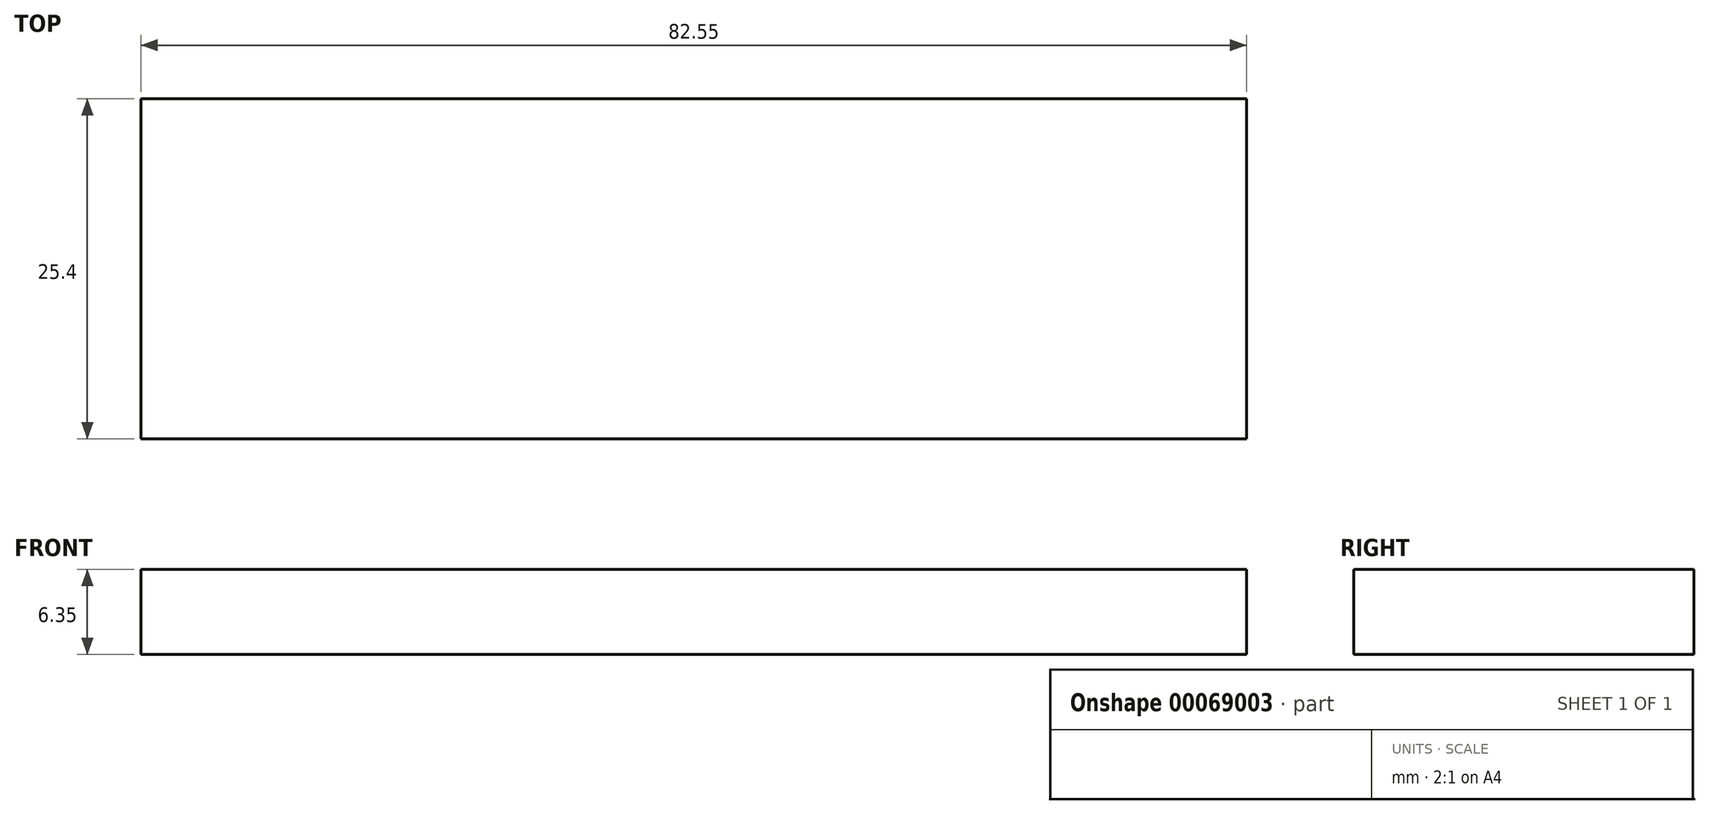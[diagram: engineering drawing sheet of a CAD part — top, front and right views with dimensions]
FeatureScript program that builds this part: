
annotation { "Feature Type Name" : "Feature", "Feature Type Description" : "" }
export const myFeature = defineFeature(function(context is Context, id is Id, definition is map)
    precondition{}
    {
        {
            var Q0;
            Q0=qCreatedBy(makeId("Top.planeOp"),FACE);
            var sketch = newSketch(context, id + "F0", { "sketchPlane" : qUnion([Q0])});
            skLineSegment(sketch, "E0.bottom", {"start": v(-45.02, 11.49) * mm, "end": v(37.53, 11.49) * mm});
            skLineSegment(sketch, "E0.top", {"start": v(-45.02, -13.91) * mm, "end": v(37.53, -13.91) * mm});
            skLineSegment(sketch, "E0.left", {"start": v(-45.02, 11.49) * mm, "end": v(-45.02, -13.91) * mm});
            skLineSegment(sketch, "E0.right", {"start": v(37.53, 11.49) * mm, "end": v(37.53, -13.91) * mm});
            skPoint(sketch, "E1", {"position": v(-45.02, 11.49) * mm});
            skSolve(sketch);
        }
        {
            var Q0;
            Q0 = qSketchRegion(id + "F0", true);
            extrude(context, id + "F1", {"entities" : qUnion([Q0]), "depth" : 6.35 * mm});
        }
    });
